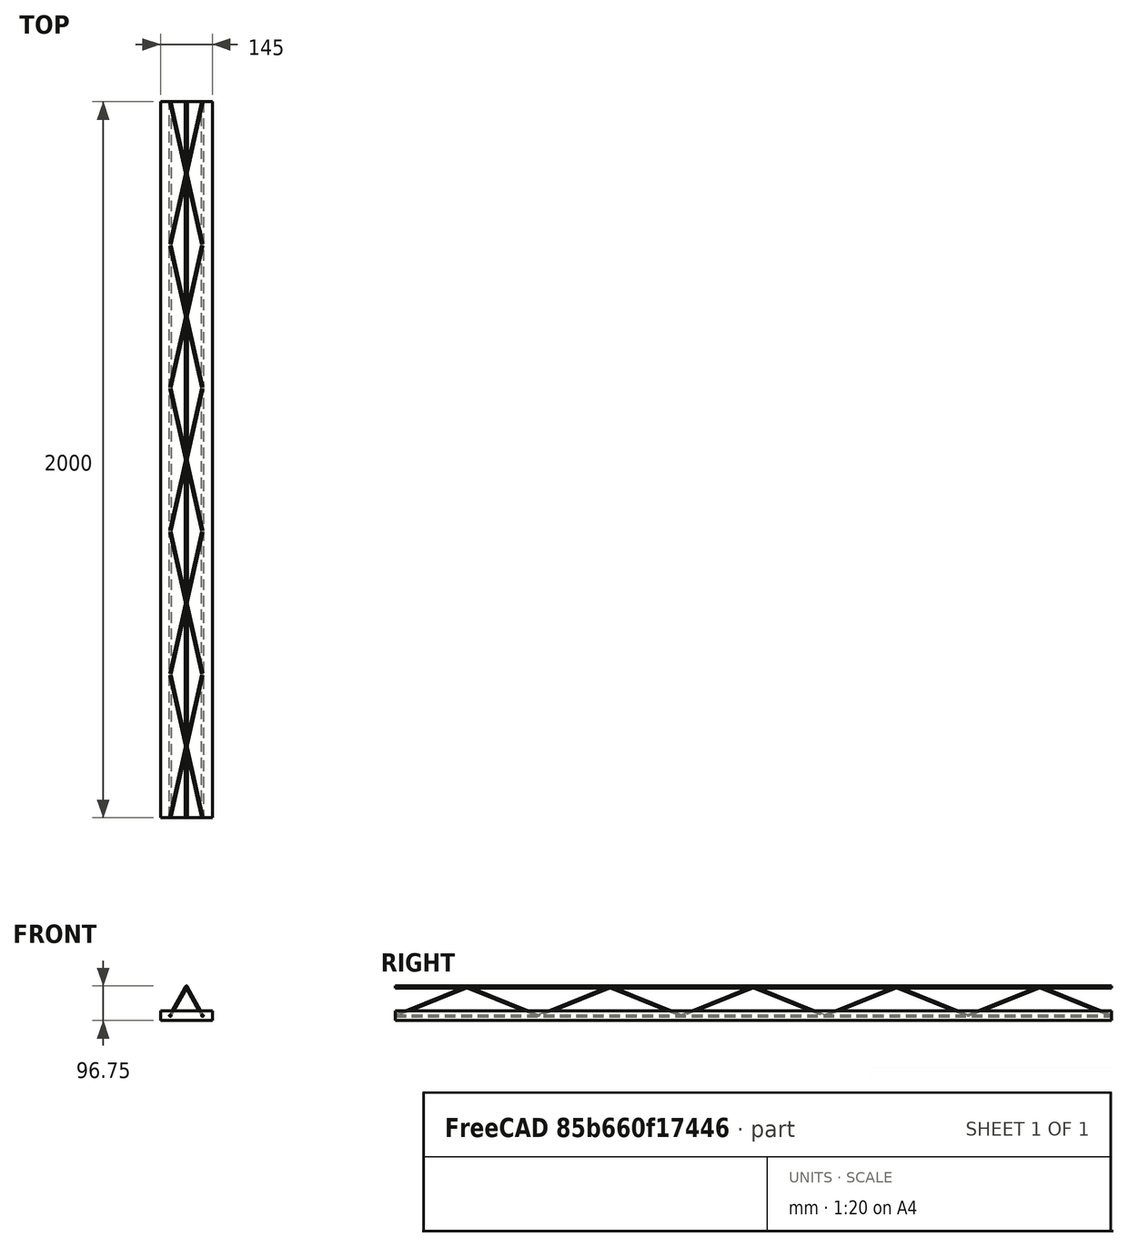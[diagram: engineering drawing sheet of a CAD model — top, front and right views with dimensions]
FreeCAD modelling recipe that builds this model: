
FCSTD DOCUMENT  (FreeCAD 1.0R38641 +468 (Git))
Label: VigaTreliçada_BIM_Parametrico
License: All rights reserved
objects: Sketcher::SketchObject×6, PartDesign::Pad×5, PartDesign::Body×5, Part::FeaturePython×4, PartDesign::Plane×3, Part::Compound×3, Spreadsheet::Sheet×2, PartDesign::Chamfer×1, PartDesign::Mirrored×1
note: 45 computed .brp shape members not serialized (recipe doc carries the construction recipe); baked Part::Feature solids carry a one-line shape summary decoded from their .brp

FEATURE [Sketcher::SketchObject] Sketch010  label="Trelica001"
  ArcFitTolerance = 1e-06
  AttachmentSupport = -> [XZ_Plane008]
  FullyConstrained = true
  MakeInternals = false
  MapMode = 5
  Placement = pos=(0,0,0) rot=(1,0,0;1.5708rad)
  expr: .Constraints.banzo_inf = <<Gerdau_Models>>.banzo_inf
  expr: Constraints[2] = <<Gerdau_Models>>.dist_banz_inf / 2
  sketch-geometry (1):
    g0: Circle CenterX=-45 CenterY=0 CenterZ=0 NormalX=0 NormalY=0 NormalZ=1 AngleXU=0 Radius=2.5
  constraints (3):
    c: Diameter(g0) = 5  'banzo_inf'
    c: PointOnObject(g0,g-1)
    c: DistanceX(g0,g-1) = 45
FEATURE [PartDesign::Pad] Pad008
  Direction = (0,-1,2e-16)
  Length = 2000
  Length2 = 10
  Placement = pos=(0,0,0) rot=(1,0,0;1.5708rad)
  Profile = -> Sketch010
  ReferenceAxis = -> Sketch010 [N_Axis]
  Refine = true
  Suppressed = false
  Type = 0
  expr: Length = <<Dimentions>>.comprimento
FEATURE [PartDesign::Body] Body008  label="Banzo_Inf_003"
  AllowCompound = false
  Group = -> [Sketch010,Pad008]
  Origin = -> Origin008
  Tip = -> Pad008
FEATURE [Sketcher::SketchObject] Sketch011
  ArcFitTolerance = 1e-06
  AttachmentSupport = -> [Sketch010]
  FullyConstrained = true
  MakeInternals = false
  MapMode = 2
  Placement = pos=(0,0,0) rot=(1,0,0;1.5708rad)
  expr: Constraints[0] = <<Gerdau_Models>>.banzo_inf
  expr: Constraints[2] = <<Gerdau_Models>>.dist_banz_inf / 2
  sketch-geometry (1):
    g0: Circle CenterX=45 CenterY=0 CenterZ=0 NormalX=0 NormalY=0 NormalZ=1 AngleXU=0 Radius=2.5
  constraints (3):
    c: Diameter(g0) = 5
    c: PointOnObject(g0,g-1)
    c: DistanceX(g-1,g0) = 45
FEATURE [PartDesign::Pad] Pad009
  Direction = (0,-1,2e-16)
  Length = 2000
  Length2 = 10
  Placement = pos=(0,0,0) rot=(1,0,0;1.5708rad)
  Profile = -> Sketch011
  ReferenceAxis = -> Sketch011 [N_Axis]
  Refine = true
  Suppressed = false
  Type = 0
  expr: Length = <<Dimentions>>.comprimento
FEATURE [PartDesign::Body] Body009  label="Banzo_Inf_004"
  AllowCompound = false
  Group = -> [Sketch011,Pad009]
  Origin = -> Origin009
  Tip = -> Pad009
FEATURE [Sketcher::SketchObject] Sketch012
  ArcFitTolerance = 1e-06
  AttachmentSupport = -> [Sketch010]
  FullyConstrained = true
  MakeInternals = false
  MapMode = 2
  Placement = pos=(0,0,0) rot=(1,0,0;1.5708rad)
  expr: Constraints[1] = <<Gerdau_Models>>.banzo_sup
  expr: Constraints[2] = <<Gerdau_Models>>.altura * 10
  sketch-geometry (1):
    g0: Circle CenterX=0 CenterY=80 CenterZ=0 NormalX=0 NormalY=0 NormalZ=1 AngleXU=0 Radius=3
  constraints (3):
    c: PointOnObject(g0,g-2)
    c: Diameter(g0) = 6
    c: DistanceY(g-1,g0) = 80
FEATURE [PartDesign::Pad] Pad010
  Direction = (0,-1,2e-16)
  Length = 2000
  Length2 = 10
  Placement = pos=(0,0,0) rot=(1,0,0;1.5708rad)
  Profile = -> Sketch012
  ReferenceAxis = -> Sketch012 [N_Axis]
  Refine = true
  Suppressed = false
  Type = 0
  expr: Length = <<Dimentions>>.comprimento
FEATURE [PartDesign::Plane] DatumPlane003
  AttachmentOffset = pos=(0,0,45) rot=(0,1,0;0.512389rad)
  AttachmentSupport = -> [Pad010]
  Length = 216.647
  MapMode = 4
  Placement = pos=(45,0,-1e-14) rot=(0.504846,0,0.863209;3.14159rad)
  ResizeMode = 0
  Width = 2123.02
  expr: .AttachmentOffset.Base.z = <<Gerdau_Models>>.dist_banz_inf / 2
  expr: .AttachmentOffset.Rotation.Pitch = atan(<<Gerdau_Models>>.dist_banz_inf / 2 / (<<Gerdau_Models>>.altura * 10))
FEATURE [PartDesign::Body] Body010  label="Banzo_sup001"
  AllowCompound = false
  Group = -> [Sketch012,Pad010,DatumPlane003]
  Origin = -> Origin010
  Tip = -> Pad010
FEATURE [Sketcher::SketchObject] Sketch013
  ArcFitTolerance = 1e-06
  AttachmentSupport = -> [DatumPlane003]
  ExternalGeometry = -> [Pad009,Pad010]
  FullyConstrained = true
  MakeInternals = false
  MapMode = 5
  Placement = pos=(45,0,-1.07e-14) rot=(0.504846,0,0.863209;3.14159rad)
  expr: Constraints[2] = <<Gerdau_Models>>.dist_diagonal
  expr: Constraints[9] = <<Gerdau_Models>>.dist_diagonal * 2
  sketch-geometry (3):
    g0: LineSegment StartX=8.9e-15 StartY=0 StartZ=0 EndX=91.7878 EndY=200 EndZ=0
    g1: LineSegment StartX=91.7878 StartY=-2.84e-14 StartZ=0 EndX=91.7878 EndY=200 EndZ=0
    g2: LineSegment StartX=1.07e-14 StartY=400 StartZ=0 EndX=91.7878 EndY=200 EndZ=0
  constraints (10):
    c: Symmetric(g-3,g-3,g0)
    c: Vertical(g1)
    c: DistanceY(g1,g1) = 200
    c: DistanceY(g0,g1) = 0
    c: DistanceX(g0,g1) = 0
    c: Symmetric(g-4,g-4,g1)
    c: DistanceX(g2,g0) = 0
    c: DistanceX(g2,g0) = 0
    c: DistanceY(g0,g2) = 0
    c: DistanceY(g-3,g2) = 400
FEATURE [PartDesign::Plane] DatumPlane004
  AttachmentSupport = -> [Sketch013]
  Length = 217.963
  MapMode = 7
  Placement = pos=(45,0,-2.7e-15) rot=(0.09136,0.822241,0.561758;3.01692rad)
  ResizeMode = 0
  Width = 227.355
FEATURE [PartDesign::Plane] DatumPlane005
  AttachmentSupport = -> [Sketch013]
  Length = 217.963
  MapMode = 7
  Placement = pos=(45,-400,-2.84e-14) rot=(0.991067,0.110119,0.075233;1.95121rad)
  ResizeMode = 0
  Width = 227.355
FEATURE [Sketcher::SketchObject] Sketch014
  ArcFitTolerance = 1e-06
  AttachmentSupport = -> [DatumPlane004]
  FullyConstrained = true
  MakeInternals = false
  MapMode = 5
  Placement = pos=(45,-1.8e-15,-3.1e-15) rot=(0.09136,0.822241,0.561758;3.01692rad)
  expr: Constraints[1] = <<Gerdau_Models>>.diagonal
  sketch-geometry (1):
    g0: Circle CenterX=0 CenterY=0 CenterZ=0 NormalX=0 NormalY=0 NormalZ=1 AngleXU=0 Radius=2.1
  constraints (2):
    c: Coincident(g0,g-1)
    c: Diameter(g0) = 4.2
FEATURE [PartDesign::Pad] Pad011
  Direction = (0.204493,0.908856,-0.363542)
  Length = 10
  Length2 = 10
  Placement = pos=(45,0,-2.7e-15) rot=(0.09136,0.822241,0.561758;3.01692rad)
  Profile = -> Sketch014
  ReferenceAxis = -> Sketch014 [N_Axis]
  Refine = true
  Suppressed = false
  Type = 3
  UpToFace = -> Pad010 [Face1]
FEATURE [PartDesign::Chamfer] Chamfer001
  Angle = 45
  Base = -> Pad011 [Face2]
  BaseFeature = -> Pad011
  ChamferType = 0
  FlipDirection = false
  Placement = pos=(45,0,-2.7e-15) rot=(0.09136,0.822241,0.561758;3.01692rad)
  Refine = true
  Size = 2.1
  Size2 = 1
  SupportTransform = false
  Suppressed = false
  UseAllEdges = false
  expr: Size = <<Gerdau_Models>>.diagonal / 2
FEATURE [PartDesign::Mirrored] Mirrored002
  BaseFeature = -> Chamfer001
  MirrorPlane = -> YZ_Plane011
  Placement = pos=(45,0,-2.7e-15) rot=(0.09136,0.822241,0.561758;3.01692rad)
  Refine = true
  Suppressed = false
  TransformMode = 1
FEATURE [PartDesign::Body] Body011  label="Diagonal_002"
  AllowCompound = false
  Group = -> [Sketch013,DatumPlane004,Sketch014,Pad011,Chamfer001,Mirrored002,DatumPlane005]
  Origin = -> Origin011
  Tip = -> Mirrored002
FEATURE [Part::Compound] Compound004  label="Compound005"
  Links = -> [Body011]
FEATURE [Part::FeaturePython] Array004  # Draft array (typed FeaturePython)
  AlwaysSyncPlacement = false
  Angle = 360
  ArrayType = 0
  Axis = (0,0,1)
  Base = -> Compound004
  Center = (0,0,0)
  Count = 5
  ExpandArray = false
  Fuse = false
  IntervalAxis = (0,0,0)
  IntervalX = (200,0,0)
  IntervalY = (0,-400,0)
  IntervalZ = (0,0,100)
  NumberCircles = 3
  NumberPolar = 5
  NumberX = 1
  NumberY = 5
  NumberZ = 1
  PlacementList = 5 placements: arithmetic series from (0,0,0) step (0,-400,0) to (0,-1600,0)
  RadialDistance = 50
  ScaleList = (5) [(1,1,1),(1,1,1),(1,1,1),(1,1,1),(1,1,1)]
  Symmetry = 1
  TangentialDistance = 25
  expr: .IntervalY.y = -<<Gerdau_Models>>.dist_diagonal * 2
  expr: NumberY = trunc((<<Dimentions>>.comprimento + <<Gerdau_Models>>.dist_diagonal) / (<<Gerdau_Models>>.dist_diagonal * 2))
FEATURE [Part::FeaturePython] Clone001  label="Compound003"  # Draft clone (typed FeaturePython)
  AttacherType = Attacher::AttachEngine3D
  Fuse = false
  Objects = -> [Compound004]
  Placement = pos=(0,-400,0) rot=(0,0,1;3.14159rad)
  Scale = (1,1,1)
  expr: .Placement.Base.y = -2 * <<Gerdau_Models>>.dist_diagonal
FEATURE [Part::FeaturePython] Array005  # Draft array (typed FeaturePython)
  AlwaysSyncPlacement = false
  Angle = 360
  ArrayType = 0
  Axis = (0,0,1)
  Base = -> Clone001
  Center = (0,0,0)
  Count = 5
  ExpandArray = false
  Fuse = false
  IntervalAxis = (0,0,0)
  IntervalX = (100,0,0)
  IntervalY = (0,-400,0)
  IntervalZ = (0,0,100)
  NumberCircles = 3
  NumberPolar = 5
  NumberX = 1
  NumberY = 5
  NumberZ = 1
  PlacementList = 5 placements: arithmetic series from (0,-400,0) step (0,-400,0) to (0,-2000,0)
  RadialDistance = 50
  ScaleList = (5) [(1,1,1),(1,1,1),(1,1,1),(1,1,1),(1,1,1)]
  Symmetry = 1
  TangentialDistance = 25
  expr: .IntervalY.y = -<<Gerdau_Models>>.dist_diagonal * 2
  expr: NumberY = trunc(<<Dimentions>>.comprimento / (<<Gerdau_Models>>.dist_diagonal * 2))
FEATURE [Sketcher::SketchObject] Sketch015
  ArcFitTolerance = 1e-06
  AttachmentSupport = -> [XY_Plane012]
  ExternalGeometry = -> [Pad009,Sketch010,Pad008]
  FullyConstrained = true
  MakeInternals = false
  MapMode = 5
  expr: Constraints[10] = <<Dimentions>>.cobrimento
  expr: Constraints[11] = <<Dimentions>>.cobrimento
  expr: Constraints[8] = <<Dimentions>>.comprimento
  sketch-geometry (4):
    g0: LineSegment StartX=-72.5 StartY=-2000 StartZ=0 EndX=-72.5 EndY=0 EndZ=0
    g1: LineSegment StartX=-72.5 StartY=0 StartZ=0 EndX=72.5 EndY=0 EndZ=0
    g2: LineSegment StartX=72.5 StartY=0 StartZ=0 EndX=72.5 EndY=-2000 EndZ=0
    g3: LineSegment StartX=72.5 StartY=-2000 StartZ=0 EndX=-72.5 EndY=-2000 EndZ=0
  constraints (12):
    c: Coincident(g0,g1)
    c: Coincident(g1,g2)
    c: Coincident(g2,g3)
    c: Coincident(g3,g0)
    c: Vertical(g0)
    c: Vertical(g2)
    c: Horizontal(g1)
    c: Horizontal(g3)
    c: DistanceY(g0,g0) = 2000
    c: DistanceY(g-4,g0) = 0
    c: DistanceX(g0,g-5) = 25
    c: DistanceX(g-6,g2) = 25
FEATURE [PartDesign::Pad] Pad012
  Direction = (0,0,1)
  Length = 27.5
  Length2 = 10
  Midplane = true
  Profile = -> Sketch015
  ReferenceAxis = -> Sketch015 [N_Axis]
  Refine = true
  Suppressed = false
  Type = 0
  expr: Length = <<Dimentions>>.cobrimento + <<Gerdau_Models>>.banzo_inf / 2
FEATURE [PartDesign::Body] Body012  label="Base002"
  AllowCompound = false
  Group = -> [Sketch015,Pad012]
  Origin = -> Origin012
  Tip = -> Pad012
FEATURE [Part::Compound] Compound003  label="Compound004"
  Links = -> [Body012,Body010,Body009,Body008,Array004,Array005]
FEATURE [Part::FeaturePython] Component003  label="Trelica_Gerdau_"  # Arch/BIM 119 (typed FeaturePython)
  Area = 290000
  Base = -> Compound003
  Description = Viga Trelicada
  HorizontalArea = 0
  IfcData = attributes={"GlobalId": {"name": "GlobalId", "type": "IfcGloballyUniqueId", "is_enum": false, "enum_values": []}, "Description": {"... (+480 chars omitted),+1 more (map truncated)
  IfcType = 119
  Length = 2000
  MoveBase = false
  MoveWithHost = false
  PerimeterLength = 0
  PredefinedType = 0
  VerticalArea = 0
  expr: Area = <<Dimentions>>.comprimento * (<<Gerdau_Models>>.dist_banz_inf + <<Gerdau_Models>>.banzo_inf + 2 * <<Dimentions>>.cobrimento)
  expr: Length = <<Dimentions>>.comprimento
FEATURE [Spreadsheet::Sheet] Spreadsheet005  label="Gerdau_Models"
  Design_Gerdau = 5
  cells = A1='Designação; B1='Peso (kg/m); C1='Altura (cm); D1='Banzo superior (mm); E1='Diagonal (mm); F1='Banzo inferior (mm); G1='Dist Banzo Inf (mm); H1='Dist Diagonal (mm); A2==hiddenref(Compound005.Design_Gerdau.String); B2==.B11; C2(altura)==.C11; D2(banzo_sup)==.D11; E2(diagonal)==.E11; F2(banzo_inf)==.F11; G2(dist_banz_inf)==.G11; H2(dist_diagonal)==.H11; A3='TR 12646; B3=1.016; C3=12; D3=6; E3=4.2; F3=6; G3=90; H3=400; A4='TR 16745; B4=1.032; C4=16; D4=7; E4=4.2; F4=5; G4=90; H4=200; A5='TR 16746; B5=1.168; C5=16; D5=7; E5=4.2; F5=6; G5=90; H5=200; A6='TR 20745; B6=1.111; C6=20; D6=7; E6=4.2; F6=5; G6=90; H6=200; A7='TR 20756; B7=1.446; C7=20; D7=7; E7=5; F7=6; G7=90; H7=200; A8='TR 25856; B8=1.686; C8=25; D8=8; E8=5; F8=6; G8=90; H8=200; A9='TR 25857; B9=1.855; C9=25; D9=8; E9=5; F9=7; G9=90; H9=200; A10='TR 08644; B10=0.735; C10=8; D10=6; E10=4.2; F10=4.2; G10=90; H10=200; A11='TR 08645; B11=0.821; C11=8; D11=6; E11=4.2; F11=5; G11=90; H11=200
  expr: .Design_Gerdau.Enum = cells[<<A3:|>>]
  expr: .cells.Bind.B2.ZZ2 = tuple(.cells; <<B>> + str(hiddenref(Compound005.Design_Gerdau) + 3); <<ZZ>> + str(hiddenref(Compound005.Design_Gerdau) + 3))
FEATURE [Spreadsheet::Sheet] Spreadsheet006  label="Dimentions"
  cells = A1='Comprimento (mm); B1='Cobrimento (mm); A2(comprimento)=2000; B2(cobrimento)=25
FEATURE [Part::Compound] Compound005  label="Trelica_Gerdau"
  Area = 290000
  Design_Gerdau = 8
  Length = 200
  Links = -> [Component003,Spreadsheet005,Spreadsheet006]
  expr: .Design_Gerdau.Enum = Spreadsheet005.cells[<<A3:|>>]
  expr: Area = <<Dimentions>>.comprimento * (<<Gerdau_Models>>.dist_banz_inf + <<Gerdau_Models>>.banzo_inf + 2 * <<Dimentions>>.cobrimento)
  expr: Length = 200 mm
